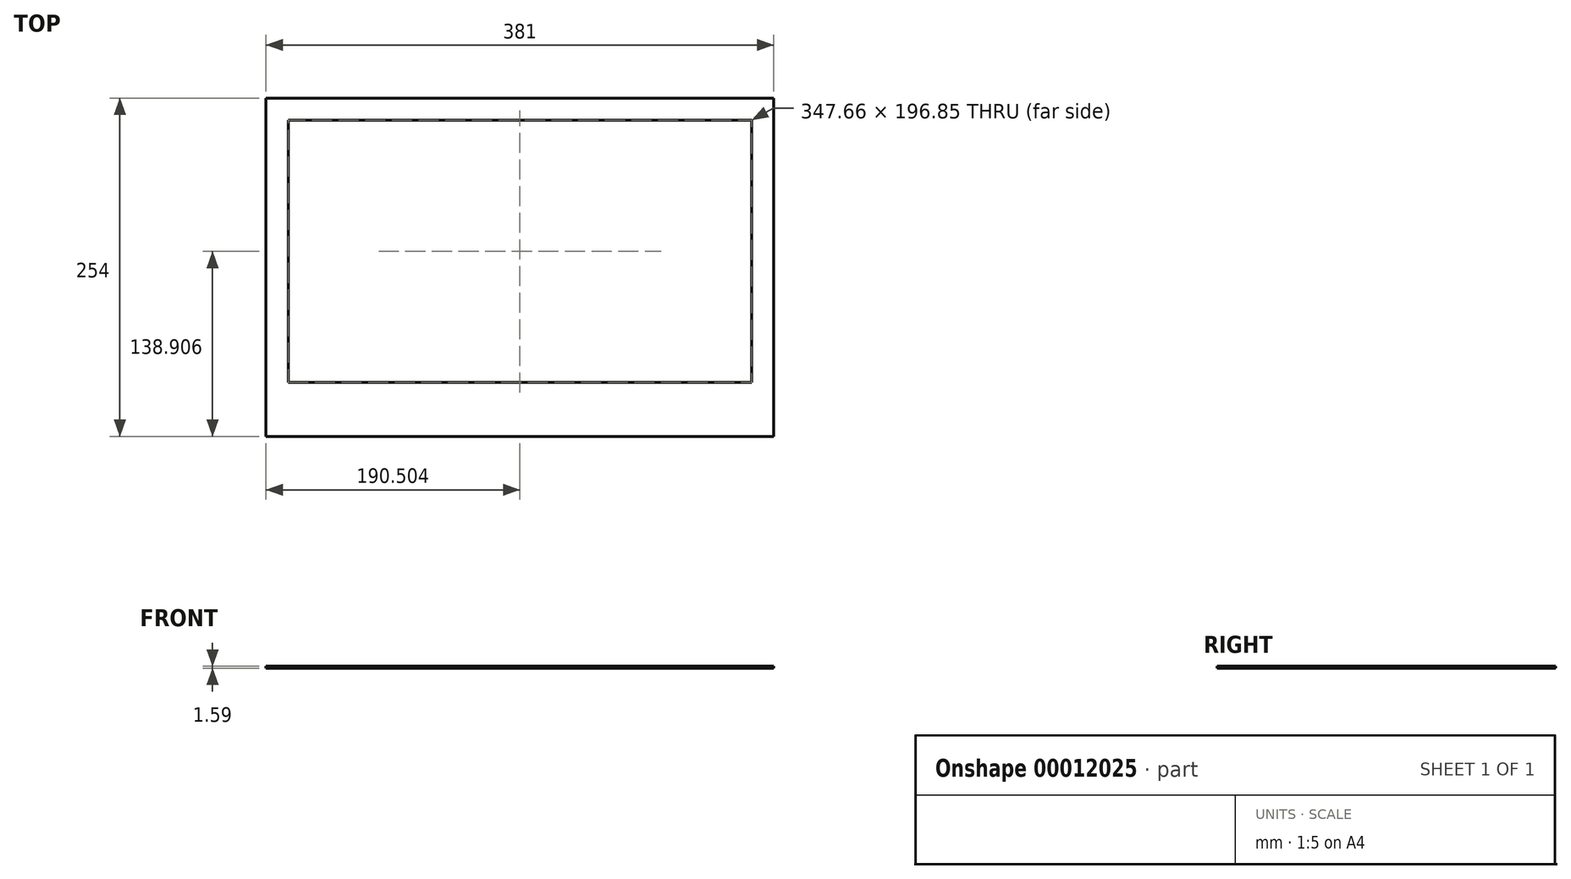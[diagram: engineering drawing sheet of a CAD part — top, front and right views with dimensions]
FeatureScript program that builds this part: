
annotation { "Feature Type Name" : "Feature", "Feature Type Description" : "" }
export const myFeature = defineFeature(function(context is Context, id is Id, definition is map)
    precondition{}
    {
        {
            var Q0;
            Q0=qCreatedBy(makeId("Top.planeOp"),FACE);
            var sketch = newSketch(context, id + "F0", { "sketchPlane" : qUnion([Q0])});
            skLineSegment(sketch, "E0.rect.bottom", {"start": v(202.54, 127) * mm, "end": v(-178.46, 127) * mm});
            skLineSegment(sketch, "E0.rect.top", {"start": v(202.54, -127) * mm, "end": v(-178.46, -127) * mm});
            skLineSegment(sketch, "E0.rect.left", {"start": v(202.54, 127) * mm, "end": v(202.54, -127) * mm});
            skLineSegment(sketch, "E0.rect.right", {"start": v(-178.46, 127) * mm, "end": v(-178.46, -127) * mm});
            skLineSegment(sketch, "E1.bottom", {"start": v(-168.14, 116.68) * mm, "end": v(192.22, 116.68) * mm});
            skLineSegment(sketch, "E1.top", {"start": v(-168.14, -92.87) * mm, "end": v(192.22, -92.87) * mm});
            skLineSegment(sketch, "E1.left", {"start": v(-168.14, 116.68) * mm, "end": v(-168.14, -92.87) * mm});
            skLineSegment(sketch, "E1.right", {"start": v(192.22, 116.68) * mm, "end": v(192.22, -92.87) * mm});
            skLineSegment(sketch, "E2.bottom", {"start": v(-161.79, 110.33) * mm, "end": v(185.87, 110.33) * mm});
            skLineSegment(sketch, "E2.top", {"start": v(-161.79, -86.52) * mm, "end": v(185.87, -86.52) * mm});
            skLineSegment(sketch, "E2.left", {"start": v(-161.79, 110.33) * mm, "end": v(-161.79, -86.52) * mm});
            skLineSegment(sketch, "E2.right", {"start": v(185.87, 110.33) * mm, "end": v(185.87, -86.52) * mm});
            skSolve(sketch);
        }
        {
            var Q0;
            Q0=makeQuery(id+"F0.imprint","IMPRINT",FACE,{"disambiguationData":[TD([[makeQuery(id+"F0.imprint","IMPRINT",EDGE,{"derivedFrom":sQuery(id+"F0.wireOp",EDGE,"E0.rect.bottom")}),1.0]])]});
            var Q1;
            Q1=makeQuery(id+"F0.imprint","IMPRINT",FACE,{"disambiguationData":[TD([[makeQuery(id+"F0.imprint","IMPRINT",EDGE,{"derivedFrom":sQuery(id+"F0.wireOp",EDGE,"E1.bottom")}),-1.0]])]});
            extrude(context, id + "F1", {"entities" : qUnion([Q0, Q1]), "depth" : 1.59 * mm});
        }
    });
